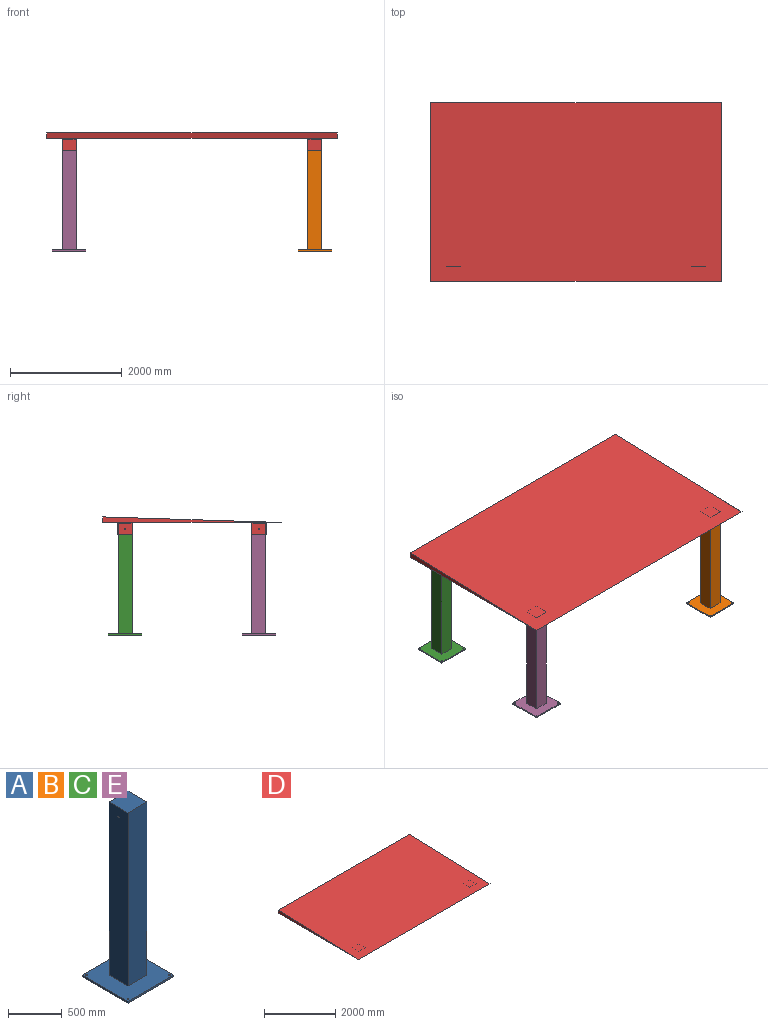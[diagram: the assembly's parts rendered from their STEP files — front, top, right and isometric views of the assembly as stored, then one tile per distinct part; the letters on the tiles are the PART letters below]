
ASSEMBLY  parts=5 mates=6
PART A: 16 faces, bbox 600x600x2000 mm
  f0: plane 600x20mm, normal (0,1,0), area 12000mm2, adj f1,f3,f8,f9
  f1: plane 600x20mm, normal (-1,0,0), area 12000mm2, adj f0,f2,f8,f9
  f2: plane 600x20mm, normal (0,-1,0), area 12000mm2, adj f1,f3,f8,f9
  f3: plane 600x20mm, normal (1,0,0), area 12000mm2, adj f0,f2,f8,f9
  f4: cylinder r=7.5mm len=20mm, axis (0,0,-1), area 942.5mm2, adj f8,f9
  f5: cylinder r=7.5mm len=20mm, axis (0,0,-1), area 942.5mm2, adj f8,f9
  f6: cylinder r=7.5mm len=20mm, axis (0,0,-1), area 942.5mm2, adj f8,f9
  f7: cylinder r=7.5mm len=20mm, axis (0,0,-1), area 942.5mm2, adj f8,f9
  f8: plane 600x600mm, normal (0,0,1), area 296793.1mm2, adj f0,f1,f2,f3,f4,f5,f6,f7
  f9: plane 600x600mm, normal (0,0,-1), area 359293.1mm2, adj f0,f1,f2,f3,f4,f5,f6,f7
  f10: plane 250x250mm, normal (0,0,1), area 62500mm2, adj f11,f12,f13,f14
  f11: plane 1980x250mm, normal (0,-1,0), area 495000mm2, adj f8,f10,f12,f14
  f12: plane 1980x250mm, normal (-1,0,0), area 494823.3mm2, adj f8,f10,f11,f13,f15
  f13: plane 1980x250mm, normal (0,1,0), area 495000mm2, adj f8,f10,f12,f14
  f14: plane 1980x250mm, normal (1,0,0), area 494823.3mm2, adj f8,f10,f11,f13,f15
  f15: cylinder r=7.5mm len=250mm, axis (1,0,0), area 11781mm2, adj f12,f14
PART B: same geometry as A
PART C: same geometry as A
PART D: 53 faces, bbox 5200x3200x315 mm
  f0: plane 255x255mm, normal (0,0,-1), area 2525mm2, adj f13,f14,f15,f16,f33,f34,f35,f36
  f1: plane 255x255mm, normal (0,0,-1), area 2525mm2, adj f17,f18,f19,f20,f38,f39,f40,f41
  f2: plane 255x255mm, normal (0,0,-1), area 2525mm2, adj f21,f22,f23,f24,f43,f44,f45,f46
  f3: plane 255x255mm, normal (0,0,-1), area 2525mm2, adj f25,f26,f27,f28,f48,f49,f50,f51
  f4: cylinder r=7.5mm len=15mm, axis (-1,0,0), area 117.8mm2, adj f25,f48
  f5: cylinder r=7.5mm len=15mm, axis (-1,0,0), area 117.8mm2, adj f21,f43
  f6: cylinder r=7.5mm len=15mm, axis (-1,0,0), area 117.8mm2, adj f17,f38
  f7: cylinder r=7.5mm len=15mm, axis (-1,0,0), area 117.8mm2, adj f13,f33
  f8: plane 3200x100mm, normal (1,0,0), area 160000mm2, adj f10,f11,f12
  f9: plane 3200x100mm, normal (-1,0,0), area 160000mm2, adj f10,f11,f12
  f10: plane 5200x100mm, normal (0,1,0), area 520000mm2, adj f8,f9,f11,f12
  f11: plane 5200x3200mm, normal (0,0,-1), area 16379900mm2, adj f8,f9,f10,f12,f13,f14,f15,f16
  f12: plane 5200x3200mm, normal (0,-0.03,1), area 16648123mm2, adj f8,f9,f10,f11
  f13: plane 255x215mm, normal (1,0,0), area 54648.3mm2, adj f0,f7,f11,f14,f16
  f14: plane 255x215mm, normal (0,-1,0), area 54825mm2, adj f0,f11,f13,f15
  f15: plane 255x215mm, normal (-1,0,0), area 54648.3mm2, adj f0,f11,f14,f16,f32
  f16: plane 255x215mm, normal (0,1,0), area 54825mm2, adj f0,f11,f13,f15
  f17: plane 255x215mm, normal (1,0,0), area 54648.3mm2, adj f1,f6,f11,f18,f20
  f18: plane 255x215mm, normal (0,-1,0), area 54825mm2, adj f1,f11,f17,f19
  f19: plane 255x215mm, normal (-1,0,0), area 54648.3mm2, adj f1,f11,f18,f20,f31
  f20: plane 255x215mm, normal (0,1,0), area 54825mm2, adj f1,f11,f17,f19
  f21: plane 255x215mm, normal (1,0,0), area 54648.3mm2, adj f2,f5,f11,f22,f24
  f22: plane 255x215mm, normal (0,-1,0), area 54825mm2, adj f2,f11,f21,f23
  f23: plane 255x215mm, normal (-1,0,0), area 54648.3mm2, adj f2,f11,f22,f24,f30
  f24: plane 255x215mm, normal (0,1,0), area 54825mm2, adj f2,f11,f21,f23
  f25: plane 255x215mm, normal (1,0,0), area 54648.3mm2, adj f3,f4,f11,f26,f28
  f26: plane 255x215mm, normal (0,-1,0), area 54825mm2, adj f3,f11,f25,f27
  f27: plane 255x215mm, normal (-1,0,0), area 54648.3mm2, adj f3,f11,f26,f28,f29
  f28: plane 255x215mm, normal (0,1,0), area 54825mm2, adj f3,f11,f25,f27
  f29: cylinder r=7.5mm len=15mm, axis (-1,0,0), area 117.8mm2, adj f27,f49
  f30: cylinder r=7.5mm len=15mm, axis (-1,0,0), area 117.8mm2, adj f23,f44
  f31: cylinder r=7.5mm len=15mm, axis (-1,0,0), area 117.8mm2, adj f19,f39
  f32: cylinder r=7.5mm len=15mm, axis (-1,0,0), area 117.8mm2, adj f15,f34
  f33: plane 250x200mm, normal (-1,0,0), area 49823.3mm2, adj f0,f7,f35,f36,f37
  f34: plane 250x200mm, normal (1,0,0), area 49823.3mm2, adj f0,f32,f35,f36,f37
  f35: plane 250x200mm, normal (0,1,0), area 50000mm2, adj f0,f33,f34,f37
  f36: plane 250x200mm, normal (0,-1,0), area 50000mm2, adj f0,f33,f34,f37
  f37: plane 250x250mm, normal (0,0,-1), area 62500mm2, adj f33,f34,f35,f36
  f38: plane 250x200mm, normal (-1,0,0), area 49823.3mm2, adj f1,f6,f40,f41,f42
  f39: plane 250x200mm, normal (1,0,0), area 49823.3mm2, adj f1,f31,f40,f41,f42
  f40: plane 250x200mm, normal (0,1,0), area 50000mm2, adj f1,f38,f39,f42
  f41: plane 250x200mm, normal (0,-1,0), area 50000mm2, adj f1,f38,f39,f42
  f42: plane 250x250mm, normal (0,0,-1), area 62500mm2, adj f38,f39,f40,f41
  f43: plane 250x200mm, normal (-1,0,0), area 49823.3mm2, adj f2,f5,f45,f46,f47
  f44: plane 250x200mm, normal (1,0,0), area 49823.3mm2, adj f2,f30,f45,f46,f47
  f45: plane 250x200mm, normal (0,1,0), area 50000mm2, adj f2,f43,f44,f47
  f46: plane 250x200mm, normal (0,-1,0), area 50000mm2, adj f2,f43,f44,f47
  f47: plane 250x250mm, normal (0,0,-1), area 62500mm2, adj f43,f44,f45,f46
  f48: plane 250x200mm, normal (-1,0,0), area 49823.3mm2, adj f3,f4,f50,f51,f52
  f49: plane 250x200mm, normal (1,0,0), area 49823.3mm2, adj f3,f29,f50,f51,f52
  f50: plane 250x200mm, normal (0,1,0), area 50000mm2, adj f3,f48,f49,f52
  f51: plane 250x200mm, normal (0,-1,0), area 50000mm2, adj f3,f48,f49,f52
  f52: plane 250x250mm, normal (0,0,-1), area 62500mm2, adj f48,f49,f50,f51
PART E: same geometry as A
PLACE A t=(5830.92,3126.01,-1991.25)mm
PLACE B t=(5830.92,731.01,-1991.25)mm
PLACE C t=(1435.92,3126.01,-1991.25)mm
PLACE D t=(3700.02,1980.22,23.75)mm
PLACE E t=(1435.92,731.01,-1991.25)mm
MATE parallel E.f3 <-> C.f1  axis (1,0,0) through (1765.77,497.18,-1991.25)mm
MATE fastened D.f37 <-> E.f10  axis (0,0,-1) through (1465.77,797.18,8.75)mm
MATE parallel C.f9 <-> B.f9  axis (0,0,1) through (1765.77,2892.18,-1991.25)mm
MATE fastened A.f10 <-> D.f47  axis (0,0,1) through (5860.77,3192.18,8.75)mm
MATE fastened C.f10 <-> D.f52  axis (0,0,1) through (1465.77,3192.18,8.75)mm
MATE fastened B.f10 <-> D.f42  axis (0,0,1) through (5860.77,797.18,8.75)mm
